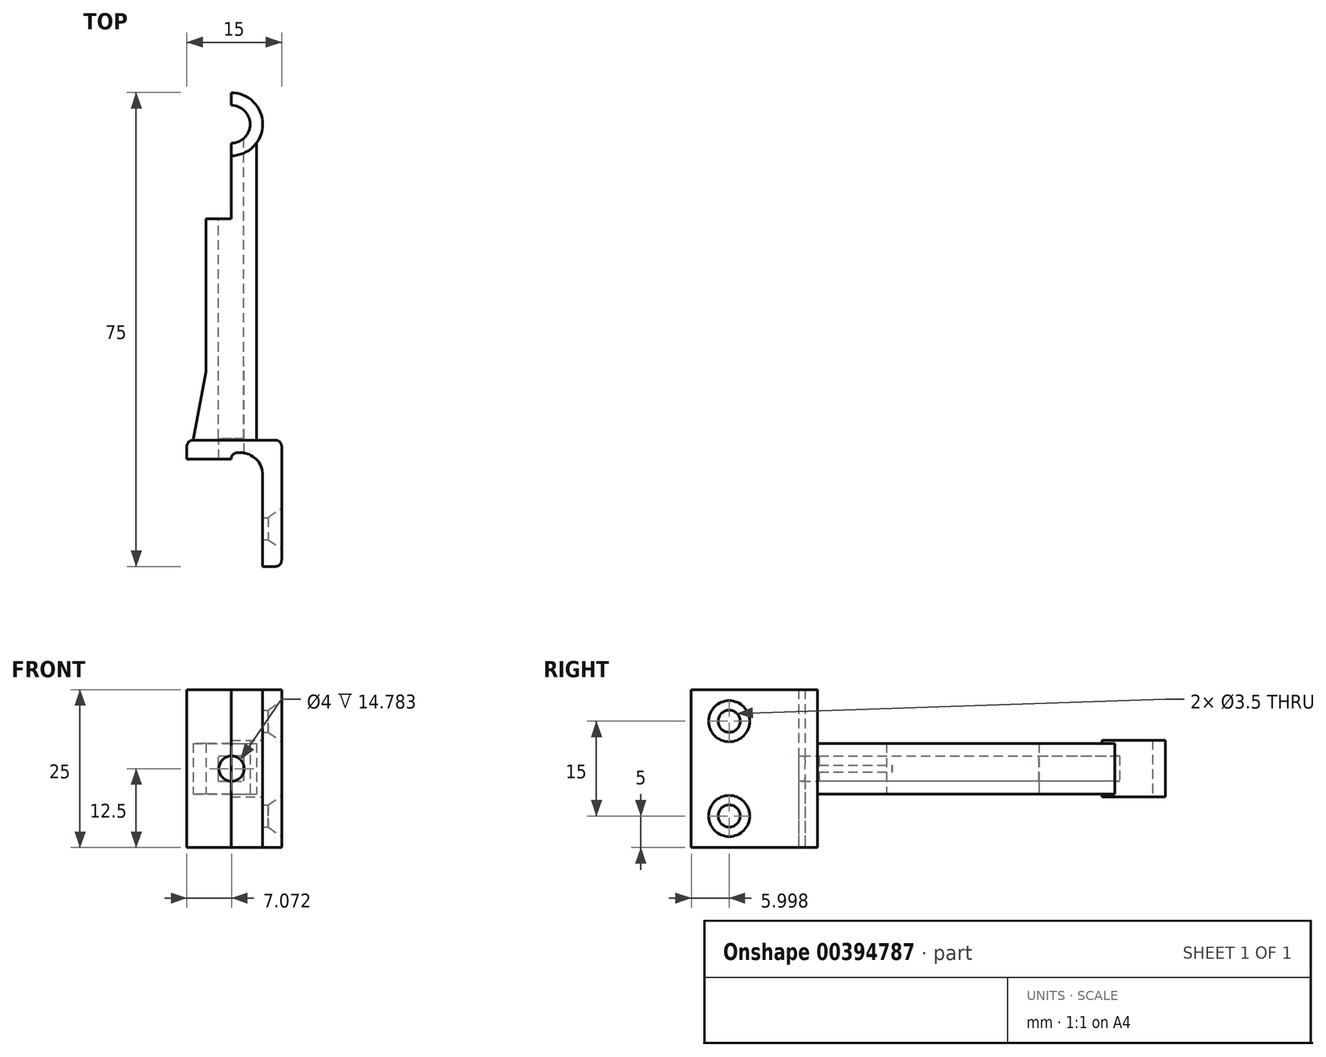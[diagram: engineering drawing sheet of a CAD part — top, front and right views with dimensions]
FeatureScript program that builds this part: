
annotation { "Feature Type Name" : "Feature", "Feature Type Description" : "" }
export const myFeature = defineFeature(function(context is Context, id is Id, definition is map)
    precondition{}
    {
        {
            var Q0;
            Q0=qCreatedBy(makeId("Top.planeOp"),FACE);
            var sketch = newSketch(context, id + "F0", { "sketchPlane" : qUnion([Q0])});
            skLineSegment(sketch, "E0", {"start": v(-8.53, -11.78) * mm, "end": v(4.47, -11.78) * mm});
            skLineSegment(sketch, "E1", {"start": v(5.47, -12.78) * mm, "end": v(5.47, -30.78) * mm});
            skLineSegment(sketch, "E2", {"start": v(4.47, -31.78) * mm, "end": v(2.47, -31.78) * mm});
            skLineSegment(sketch, "E3", {"start": v(2.47, -31.78) * mm, "end": v(2.47, -17.28) * mm});
            skLineSegment(sketch, "E4", {"start": v(-1.03, -13.78) * mm, "end": v(-1.53, -13.78) * mm});
            skLineSegment(sketch, "E5", {"start": v(-2.53, -14.78) * mm, "end": v(-2.53, -14.78) * mm});
            skLineSegment(sketch, "E6", {"start": v(-2.53, -14.78) * mm, "end": v(-9.53, -14.78) * mm});
            skLineSegment(sketch, "E7", {"start": v(-9.53, -14.78) * mm, "end": v(-9.53, -12.78) * mm});
            skPoint(sketch, "E8.visualSharp", {"position": v(2.47, -13.78) * mm});
            skArc(sketch, "E8.filletArc", {"start": v(2.47, -17.28) * mm, "mid": v(1.45, -14.8) * mm, "end": v(-1.03, -13.78) * mm});
            skPoint(sketch, "E9.visualSharp", {"position": v(-2.53, -13.78) * mm});
            skArc(sketch, "E9.filletArc", {"start": v(-1.53, -13.78) * mm, "mid": v(-2.23, -14.08) * mm, "end": v(-2.53, -14.78) * mm});
            skPoint(sketch, "E10.visualSharp", {"position": v(-9.53, -11.78) * mm});
            skArc(sketch, "E10.filletArc", {"start": v(-8.53, -11.78) * mm, "mid": v(-9.23, -12.08) * mm, "end": v(-9.53, -12.78) * mm});
            skPoint(sketch, "E11.visualSharp", {"position": v(5.47, -11.78) * mm});
            skArc(sketch, "E11.filletArc", {"start": v(5.47, -12.78) * mm, "mid": v(5.18, -12.08) * mm, "end": v(4.47, -11.78) * mm});
            skPoint(sketch, "E12.visualSharp", {"position": v(5.47, -31.78) * mm});
            skArc(sketch, "E12.filletArc", {"start": v(4.47, -31.78) * mm, "mid": v(5.18, -31.49) * mm, "end": v(5.47, -30.78) * mm});
            skLineSegment(sketch, "E13", {"start": v(1.47, -11.78) * mm, "end": v(1.47, 35.22) * mm});
            skArc(sketch, "E14", {"start": v(-2.53, 35.22) * mm, "mid": v(0.47, 38.22) * mm, "end": v(-2.53, 41.22) * mm});
            skArc(sketch, "E15", {"start": v(-2.53, 33.22) * mm, "mid": v(2.47, 38.22) * mm, "end": v(-2.53, 43.22) * mm});
            skPoint(sketch, "E16.orphan", {"position": v(1.47, 24.21) * mm});
            skPoint(sketch, "E17.orphan", {"position": v(-6.53, 24.21) * mm});
            skLineSegment(sketch, "E18", {"start": v(-2.53, 43.22) * mm, "end": v(-2.53, 23.22) * mm});
            skLineSegment(sketch, "E19", {"start": v(-2.53, 23.22) * mm, "end": v(-6.53, 23.22) * mm});
            skLineSegment(sketch, "E20", {"start": v(-6.53, 23.22) * mm, "end": v(-6.53, -0.91) * mm});
            skLineSegment(sketch, "E21", {"start": v(-6.53, -0.91) * mm, "end": v(-8.53, -11.78) * mm});
            skSolve(sketch);
        }
        {
            var Q0;
            Q0=makeQuery(id+"F0.imprint","IMPRINT",FACE,{"disambiguationData":[TD([[makeQuery(id+"F0.imprint","IMPRINT",EDGE,{"derivedFrom":sQuery(id+"F0.wireOp",EDGE,"E0")}),-1.0]])]});
            extrude(context, id + "F1", {"entities" : qUnion([Q0]), "endBound" : BoundingType.SYMMETRIC, "depth" : 25 * mm});
        }
        {
            var Q0;
            Q0=makeQuery(id+"F1.opExtrude","SWEPT_FACE",FACE,{"disambiguationData":[OSD([sQuery(id+"F0.wireOp",EDGE,"E1")])]});
            var sketch = newSketch(context, id + "F2", { "sketchPlane" : qUnion([Q0])});
            skPoint(sketch, "E22", {"position": v(-25.78, 7.5) * mm});
            skPoint(sketch, "E23", {"position": v(-25.78, -7.5) * mm});
            skSolve(sketch);
        }
        {
            var Q0;
            Q0=sQuery(id+"F2.wireOp",VERTEX,"E22");
            var Q1;
            Q1=sQuery(id+"F2.wireOp",VERTEX,"E23");
            var Q2;
            Q2=makeQuery(id+"F1.opExtrude","SWEPT_BODY",BODY,{"disambiguationData":[OSD([sQuery(id+"F0.wireOp",EDGE,"E0"),sQuery(id+"F0.wireOp",EDGE,"E1"),sQuery(id+"F0.wireOp",EDGE,"E2"),sQuery(id+"F0.wireOp",EDGE,"E3"),sQuery(id+"F0.wireOp",EDGE,"E4"),sQuery(id+"F0.wireOp",EDGE,"E6"),sQuery(id+"F0.wireOp",EDGE,"E7"),sQuery(id+"F0.wireOp",EDGE,"E8.filletArc"),sQuery(id+"F0.wireOp",EDGE,"E9.filletArc"),sQuery(id+"F0.wireOp",EDGE,"E10.filletArc"),sQuery(id+"F0.wireOp",EDGE,"E11.filletArc"),sQuery(id+"F0.wireOp",EDGE,"E12.filletArc")])]});
            hole(context, id + "F3", {"style" : HoleStyle.C_SINK, "endStyle" : HoleEndStyle.THROUGH, "holeDiameter" : 3.5 * mm, "cSinkDiameter" : 6.5 * mm, "cSinkAngle" : 70 * degree, "tappedDepth" : 12 * mm, "tapClearance" : 3, "startFromSketch" : true, "locations" : qUnion([Q0, Q1]), "scope" : qUnion([Q2])});
        }
        {
            var Q0;
            {var subQ0=sQuery(id+"F0.wireOp",EDGE,"E13");Q0=makeQuery(id+"F0.imprint","IMPRINT",FACE,{"disambiguationData":[TD([[makeQuery(id+"F0.imprint","IMPRINT",EDGE,{"derivedFrom":subQ0}),1.0]])]});}
            extrude(context, id + "F4", {"entities" : qUnion([Q0]), "operationType" : NewBodyOperationType.ADD, "endBound" : BoundingType.SYMMETRIC, "depth" : 8 * mm});
        }
        {
            var Q0;
            Q0=makeQuery(id+"F0.imprint","IMPRINT",FACE,{"disambiguationData":[TD([[makeQuery(id+"F0.imprint","IMPRINT",EDGE,{"derivedFrom":sQuery(id+"F0.wireOp",EDGE,"E14")}),-1.0]])]});
            extrude(context, id + "F5", {"entities" : qUnion([Q0]), "operationType" : NewBodyOperationType.ADD, "endBound" : BoundingType.SYMMETRIC, "depth" : 9 * mm});
        }
        {
            var Q0;
            Q0=qCreatedBy(makeId("Right.planeOp"),FACE);
            cPlane(context, id + "F6", {"entities" : qUnion([Q0]), "cplaneType" : CPlaneType.OFFSET, "offset" : 2.53 * mm, "oppositeDirection" : true, "width" : 150 * mm, "height" : 150 * mm});
        }
        {
            var Q0;
            Q0=qCreatedBy(id+"F6.planeOp",FACE);
            var sketch = newSketch(context, id + "F7", { "sketchPlane" : qUnion([Q0])});
            skLineSegment(sketch, "E24", {"start": v(36.53, -2) * mm, "end": v(-11.54, -2) * mm});
            skLineSegment(sketch, "E25", {"start": v(-11.54, -2) * mm, "end": v(-11.54, 2) * mm});
            skLineSegment(sketch, "E26", {"start": v(-11.54, 2) * mm, "end": v(36.53, 2) * mm});
            skLineSegment(sketch, "E27", {"start": v(36.53, 2) * mm, "end": v(36.53, -2) * mm});
            skSolve(sketch);
        }
        {
            var Q0;
            Q0=makeQuery(id+"F7.imprint","IMPRINT",FACE,{"disambiguationData":[TD([[makeQuery(id+"F7.imprint","IMPRINT",EDGE,{"derivedFrom":sQuery(id+"F7.wireOp",EDGE,"E24")}),-1.0]])]});
            extrude(context, id + "F8", {"entities" : qUnion([Q0]), "operationType" : NewBodyOperationType.REMOVE, "endBound" : BoundingType.SYMMETRIC, "oppositeDirection" : true, "depth" : 4 * mm});
        }
        {
            var Q0;
            Q0=qCreatedBy(makeId("Front.planeOp"),FACE);
            var sketch = newSketch(context, id + "F9", { "sketchPlane" : qUnion([Q0])});
            skCircle(sketch, "E28", {"center": v(-2.46, 0) * mm, "radius": 2 * mm});
            skSolve(sketch);
        }
        {
            var Q0;
            Q0=makeQuery(id+"F9.imprint","IMPRINT",FACE,{"disambiguationData":[TD([[makeQuery(id+"F9.imprint","IMPRINT",EDGE,{"derivedFrom":sQuery(id+"F9.wireOp",EDGE,"E28")}),1.0]])]});
            var Q1;
            Q1=sQuery(id+"F9.wireOp",EDGE,"E28");
            extrude(context, id + "F10", {"entities" : qUnion([Q0]), "operationType" : NewBodyOperationType.REMOVE, "surfaceEntities" : qUnion([Q1]), "depth" : 19.3 * mm});
        }
    });
